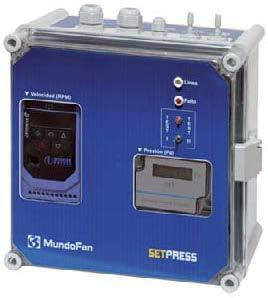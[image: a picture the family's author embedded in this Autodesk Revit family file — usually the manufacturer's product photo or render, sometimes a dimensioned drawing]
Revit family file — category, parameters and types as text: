
# Revit family: SETPRESS-075_VE10807
name_source: partatom
category: Aparatos eléctricos
revit_build: Autodesk Revit 2016 (Build: 20150220_1215(x64)
units: mm (PartAtom-declared; Revit-internal decimal feet)

## family parameters
Compartido = No
Corte con vacíos al cargar = No
Cota de conector redondo = Diámetro de uso
Mantener orientación de anotación = No
Número OmniClass = 23.80.00.00
Punto de cálculo de habitación = No
Se basa en plano de trabajo = No
Siempre vertical = Sí
Tipo de pieza = Caja de conexiones
Título OmniClass = Electric Power and Lighting

## types (1)
- SETPRESS
    Alimentación = 400Vac trifásico
    Corriente = 2,2 A
    Costo = 0 $
    Código de montaje = VE10807
    Descripción = CONTROL EFICIENCIA ENERGETICA PARA VENTILADORES
    Dimensiones máx. = 270x300x170 mm
    Fabricante = SALVADOR ESCODA
    Imagen de tipo = setpress.jpg
    Leds = linea / fallo
    Modelo = SETPRESS 0,75 kW
    Normativas = UNE-EN 12101-6
    Potencia = 0,75 kW
    Regulación = Mediante sonda analógica de presión
    Salida = 400Vac trifásico
    URL = www.salvadorescoda.com
    Visualización = frecuencia (Hz) y presión (Pa)
